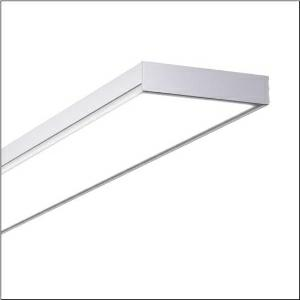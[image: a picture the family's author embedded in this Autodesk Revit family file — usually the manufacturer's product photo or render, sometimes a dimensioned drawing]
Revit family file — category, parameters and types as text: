
# Revit family: apollon_r__31_51mp26wd2341e_2cde
name_source: partatom
category: Lighting Fixtures
units: mm (PartAtom-declared; Revit-internal decimal feet)

## family parameters
Cut with Voids When Loaded = No
Host = Face
Light Source = No
Part Type = Normal
Room Calculation Point = No
Round Connector Dimension = Use Diameter
Shared = No

## types (1)
- Apollon® 31 (1 x LED, 4400 lm, 33 W, 3000K)
    Apparent Load = 33 VA
    CIE Flux Codes = 61 87 97 97 100
    Color Rendering = 80
    Color Temperature = 3000K
    Default Elevation = 1800 mm
    Description = Apollon® 31, office luminaire, primary optical cover: micro prismatic cover, of PMMA, light emission: direct distribution, primary light characteristic: symmetric, installation type: surface-mounted, LED, rated luminous flux: 4.400lm, luminous efficacy: 133lm/W, light colour: 830, colour temperature: 3000K, control gear: ECG DALI, with terminal, 5-pole, mains connection: 220..240V, AC, 50/60Hz, rated input power: 33W, housing, of sheet steel, coil coated, metallic grey (RAL 9006), length: 1.545mm, width: 200mm, height: 44mm, protection rating (complete): IP20, insulation class (complete): insulation class II (safety insulation), certification: CE, impact resistance: IK02, permissible operating ambient temperature: -20..+40°C, standard: EN 60598-2-22, packaging unit: 1 piece
    Height = 44 mm
    Lamp = 1 x LED
    Lamp Light Flux = 4400 lm
    Lamp Power = 33 W
    Lamp count = 1
    Length = 1545 mm
    Luminous efficacy = 133 lm/W
    Manufacturer = Siteco
    ModVariant = No
    Model = 51MP26WD2341E
    Mounting Place = Ceiling
    Mounting Type = Surface mounted
    Number of Poles = 1
    OnlyDefault = Yes
    Power Factor = 1
    Product Name = Apollon® 31
    Product group = office luminaire | ceiling mounted
    ProductGroupID = 302
    Protection Class = Protection class II
    Protection Degree = IP 20
    RLX_Detail_Level = 1
    RlxData = <blob elided: 24101 chars, md5=be766d14>
    Socket = socket
    Standby Power = 0 W
    System Light Flux = 4400 lm
    System Power = 33 W
    Type Comments = Product without accessories
    Type Image = l_1007091.jpg
    URL = http://relux.com
    VarID = ---
    Voltage = 0 V
    Weight = 0.00 kg
    Width = 200 mm  [stored 0.656168 ft]

note: [stored X ft] marks values corroborated as IEEE doubles in the binary element streams (Revit-internal decimal feet)

## geometry (parser evidence)
native form markers: Blend x4, Sweep x10
no freeform markers — native parametric forms only
